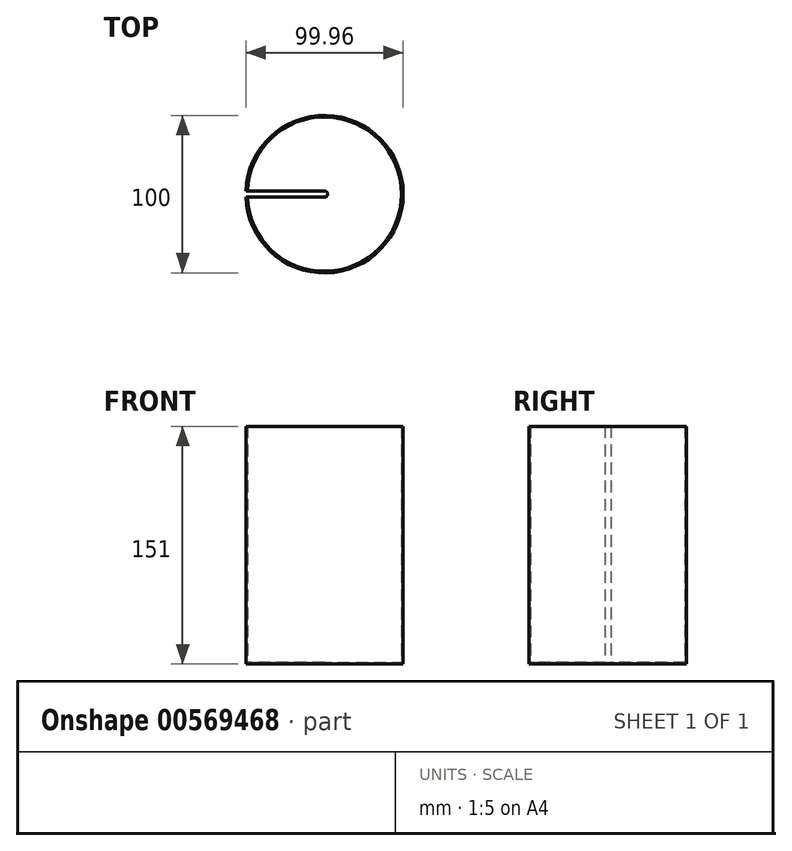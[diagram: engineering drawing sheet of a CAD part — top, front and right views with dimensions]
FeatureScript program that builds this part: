
annotation { "Feature Type Name" : "Feature", "Feature Type Description" : "" }
export const myFeature = defineFeature(function(context is Context, id is Id, definition is map)
    precondition{}
    {
        {
            var Q0;
            Q0=qCreatedBy(makeId("Top.planeOp"),FACE);
            var sketch = newSketch(context, id + "F0", { "sketchPlane" : qUnion([Q0])});
            skArc(sketch, "E0", {"start": v(-49.96, -2) * mm, "mid": v(50, 0) * mm, "end": v(-49.96, 2) * mm});
            skArc(sketch, "E1", {"start": v(0, -2) * mm, "mid": v(2, 0) * mm, "end": v(0, 2) * mm});
            skLineSegment(sketch, "E2", {"start": v(0, 0) * mm, "end": v(-50, 0) * mm, "construction": true});
            skLineSegment(sketch, "E3", {"start": v(0, 2) * mm, "end": v(-49.96, 2) * mm});
            skLineSegment(sketch, "E4", {"start": v(0, -2) * mm, "end": v(-49.96, -2) * mm});
            skSolve(sketch);
        }
        {
            var Q0;
            Q0=makeQuery(id+"F0.imprint","IMPRINT",FACE,{"disambiguationData":[TD([[makeQuery(id+"F0.imprint","IMPRINT",EDGE,{"derivedFrom":sQuery(id+"F0.wireOp",EDGE,"E0")}),1.0]])]});
            extrude(context, id + "F1", {"entities" : qUnion([Q0]), "depth" : 1 * mm, "offsetDistance" : 25 * mm});
        }
        {
            var Q0;
            Q0=makeQuery(id+"F1.opExtrude","CAP_FACE",FACE,{"disambiguationData":[OSD([sQuery(id+"F0.wireOp",EDGE,"E0"),sQuery(id+"F0.wireOp",EDGE,"E1"),sQuery(id+"F0.wireOp",EDGE,"E3"),sQuery(id+"F0.wireOp",EDGE,"E4")])],"isStart":false});
            var sketch = newSketch(context, id + "F2", { "sketchPlane" : qUnion([Q0])});
            skArc(sketch, "E5", {"start": v(-49.96, -2) * mm, "mid": v(50, 0) * mm, "end": v(-49.96, 2) * mm});
            skArc(sketch, "E6.0", {"start": v(-48.96, -2) * mm, "mid": v(49, 0) * mm, "end": v(-48.96, 2) * mm});
            skLineSegment(sketch, "E7", {"start": v(-49.96, 2) * mm, "end": v(-48.96, 2) * mm});
            skLineSegment(sketch, "E8", {"start": v(-49.96, -2) * mm, "end": v(-48.96, -2) * mm});
            skSolve(sketch);
        }
        {
            var Q0;
            Q0=makeQuery(id+"F2.imprint","IMPRINT",FACE,{"disambiguationData":[TD([[makeQuery(id+"F2.imprint","IMPRINT",EDGE,{"derivedFrom":sQuery(id+"F2.wireOp",EDGE,"E5")}),1.0]])]});
            extrude(context, id + "F3", {"entities" : qUnion([Q0]), "operationType" : NewBodyOperationType.ADD, "depth" : 150 * mm, "offsetDistance" : 25 * mm});
        }
    });
